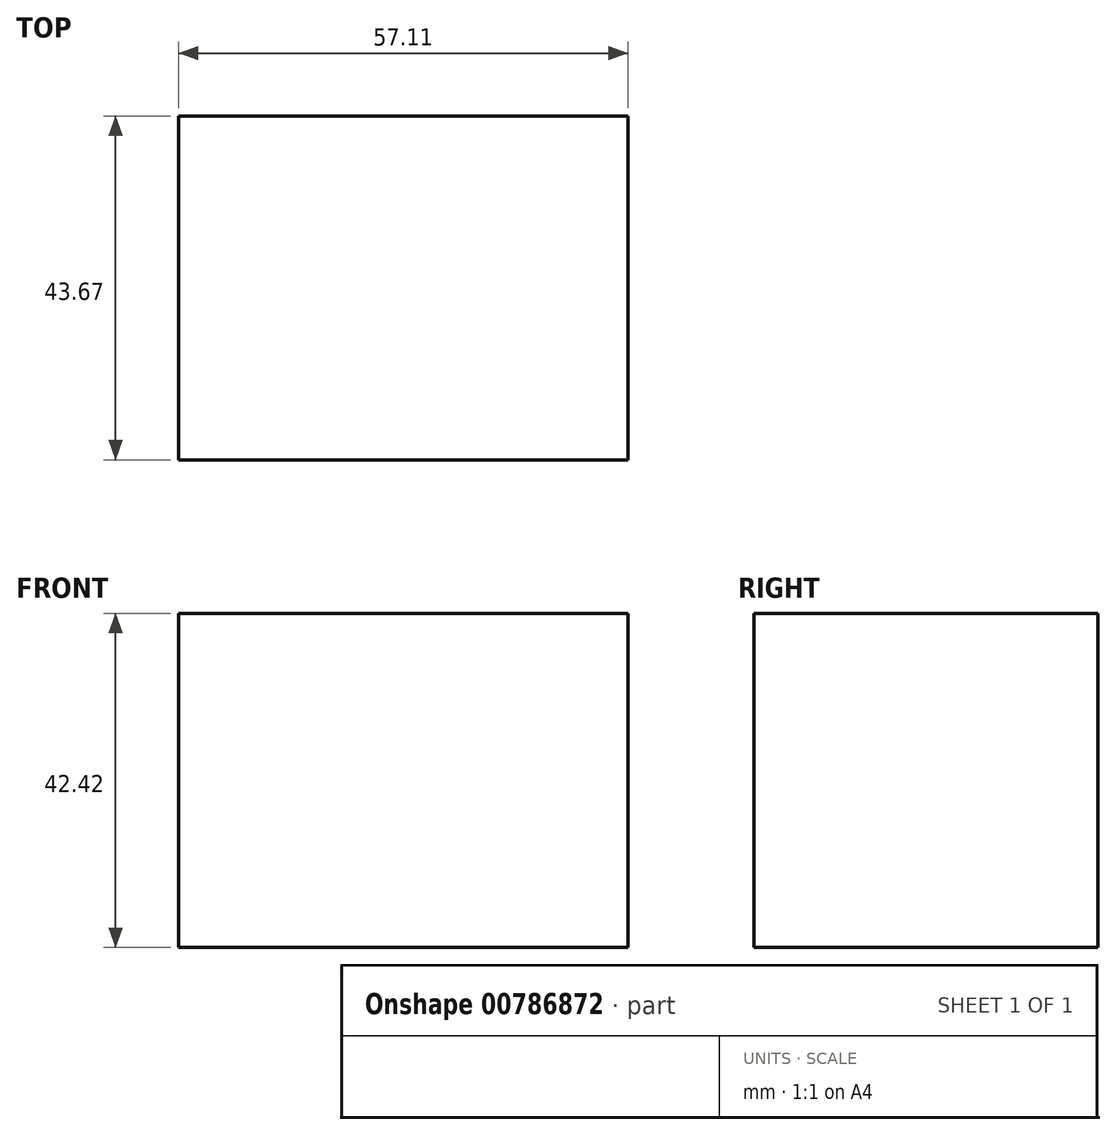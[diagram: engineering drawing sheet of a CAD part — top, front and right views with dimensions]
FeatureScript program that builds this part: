
annotation { "Feature Type Name" : "Feature", "Feature Type Description" : "" }
export const myFeature = defineFeature(function(context is Context, id is Id, definition is map)
    precondition{}
    {
        {
            var Q0;
            Q0=qCreatedBy(makeId("Top.planeOp"),FACE);
            var sketch = newSketch(context, id + "F0", { "sketchPlane" : qUnion([Q0])});
            skLineSegment(sketch, "E0.bottom", {"start": v(0, 0) * mm, "end": v(57.1, 0) * mm});
            skLineSegment(sketch, "E0.top", {"start": v(0, 43.67) * mm, "end": v(57.1, 43.67) * mm});
            skLineSegment(sketch, "E0.left", {"start": v(0, 0) * mm, "end": v(0, 43.67) * mm});
            skLineSegment(sketch, "E0.right", {"start": v(57.1, 0) * mm, "end": v(57.1, 43.67) * mm});
            skSolve(sketch);
        }
        {
            var Q0;
            Q0=makeQuery(id+"F0.imprint","IMPRINT",FACE,{"disambiguationData":[TD([[makeQuery(id+"F0.imprint","IMPRINT",EDGE,{"derivedFrom":sQuery(id+"F0.wireOp",EDGE,"E0.bottom")}),1.0]])]});
            extrude(context, id + "F1", {"entities" : qUnion([Q0]), "depth" : 42.42 * mm, "offsetDistance" : 25.4 * mm});
        }
    });
